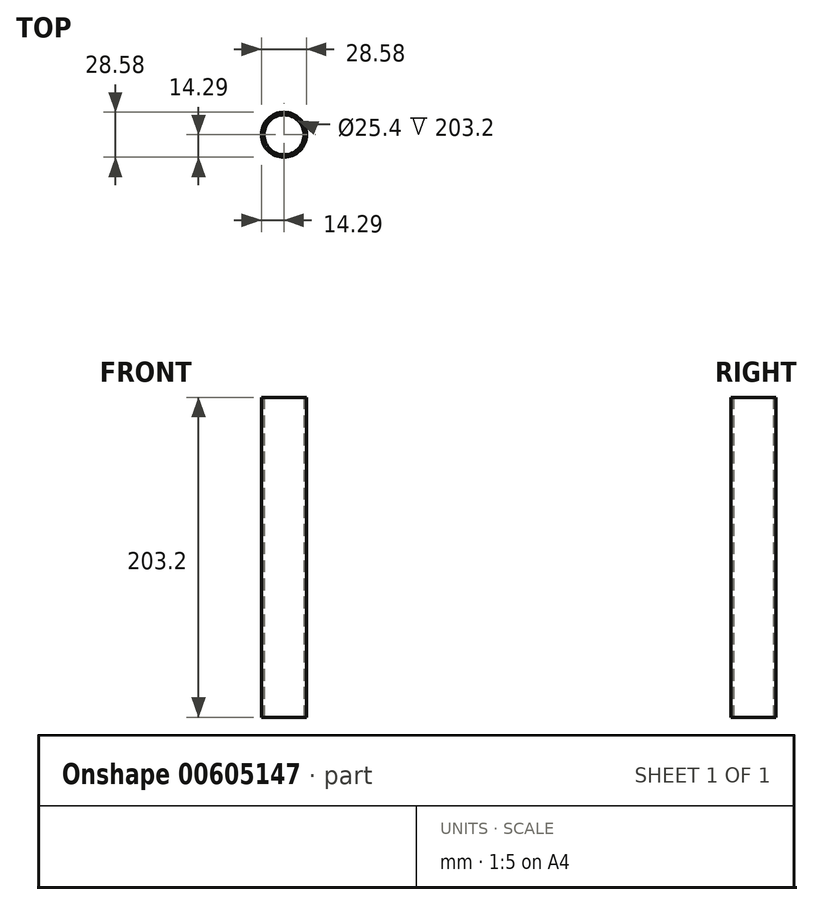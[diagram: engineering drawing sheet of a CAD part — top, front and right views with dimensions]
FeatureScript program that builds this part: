
annotation { "Feature Type Name" : "Feature", "Feature Type Description" : "" }
export const myFeature = defineFeature(function(context is Context, id is Id, definition is map)
    precondition{}
    {
        {
            var Q0;
            Q0=qCreatedBy(makeId("Top.planeOp"),FACE);
            var sketch = newSketch(context, id + "F0", { "sketchPlane" : qUnion([Q0])});
            skLineSegment(sketch, "E0", {"start": v(0, 0) * mm, "end": v(12.7, 0) * mm});
            skCircle(sketch, "E1", {"center": v(0, 0) * mm, "radius": 12.7 * mm});
            skCircle(sketch, "E2.0", {"center": v(0, 0) * mm, "radius": 14.29 * mm});
            skSolve(sketch);
        }
        {
            var Q0;
            Q0=qCreatedBy(makeId("Top.planeOp"),FACE);
            var sketch = newSketch(context, id + "F1", { "sketchPlane" : qUnion([Q0])});
            skSolve(sketch);
        }
        {
            var Q0;
            Q0=qSketchRegion(id+"F1",true);
            var Q1;
            Q1=makeQuery(id+"F0.imprint","IMPRINT",FACE,{"disambiguationData":[TD([[makeQuery(id+"F0.imprint","IMPRINT",EDGE,{"derivedFrom":sQuery(id+"F0.wireOp",EDGE,"E1")}),-1.0]])]});
            extrude(context, id + "F2", {"entities" : qUnion([Q0, Q1]), "depth" : 203.2 * mm, "offsetDistance" : 25.4 * mm});
        }
    });
